# Revit family: QF_ELECTROLUXPROFESSIONAL_1LSNJ8_IC64821LF_E
name_source: partatom
category: Attrezzature speciali
units: mm (PartAtom-declared; Revit-internal decimal feet)

## family parameters
Basato su piano di lavoro = No
Condiviso = No
Punto di calcolo locali = No
Quota connettore circolare = Usa diametro
Sempre verticale = Sì
Taglio con vuoti quando caricato = No
Tipo di parte = Normale

## types (8) — shared parameters
Cycle = 50 Hz
Depth Actual = 1110 mm  [stored 3.64173 ft]
Height Actual = 1270 mm  [stored 4.16667 ft]
Latent Heat Output = 0.0
Length Actual = 2775 mm  [stored 9.10433 ft]
Modello = IC64821LF
Phase = 3
Produttore = Electrolux Professional
Sensible Heat Output = 0.0
URL = www.electroluxprofessional.com
Volts = 400 V
Weight = 810
zero-valued in all types: Gas KW, Prospetto di default, Steam Pounds per Hour

## per-type parameters (varying)
| type | Descrizione | Item Number | Watts |
| 9882030162 | IRONER CYLINDER IC64821LF LENGTH FOLDING 2120MM PERFORMANCE EL. CE 400/50/3 DUBIXIUM FR VAC.FEED.TABLE DIAMMS | 1L0GST | 37800 W |
| 9882030309 | IRONER CYLINDER IC64821LF LENGTH FOLDING 2120MM SUPERIOR EL. CE 400/50/3 DUBIXIUM ML FEED ALONE VAC.FEED.TABLE ANTISTATI | 1L0HEA | 378000 W |
| 9882030075 | IRONER CYLINDER IC64821LF LENGTH FOLDING 2120MM SUPERIOR EL. CE 400/50/3 DUBIXIUM NO FEED ALONE VAC.FEED.TABLE ANTISTATI | 1LSP8X | 37800 W |
| 9882030161 | IRONER CYLINDER IC64821LF LENGTH FOLDING 2120MM PERFORMANCE EL. CE 400/50/3 DUBIXIUM ML VAC.FEED.TABLE DIAMMS | 1L0GSS | 37800 W |
| 9882030158 | IRONER CYLINDER IC64821LF LENGTH FOLDING 2120MM ACTIVE EL. CE 400/50/3 6MM SST CYL. ML FEED NOW | 1L0GSN | 37800 W |
| 9882030052 | IRONER CYLINDER IC64821LF LENGTH FOLDING 2120MM EL. CE 400/50/3 DUBIXIUM NO DIAMMS | 1LSP4U | 37800 W |
| 9882030306 | IRONER CYLINDER IC64821LF LENGTH FOLDING 2120MM EL. CE 400/50/3 6MM SST CYL. FR FEED ALONE VAC.FEED.TABLE | 1L0HE1 | 378000 W |
| 9882030157 | IRONER CYLINDER IC64821LF LENGTH FOLDING 2120MM ACTIVE EL. CE 400/50/3 6MM SST CYL. FR FEED NOW | 1L0GSM | 37800 W |

note: [stored X ft] marks values corroborated as IEEE doubles in the binary element streams (Revit-internal decimal feet)

## geometry (parser evidence)
native form markers: Sweep x10
no freeform markers — native parametric forms only
